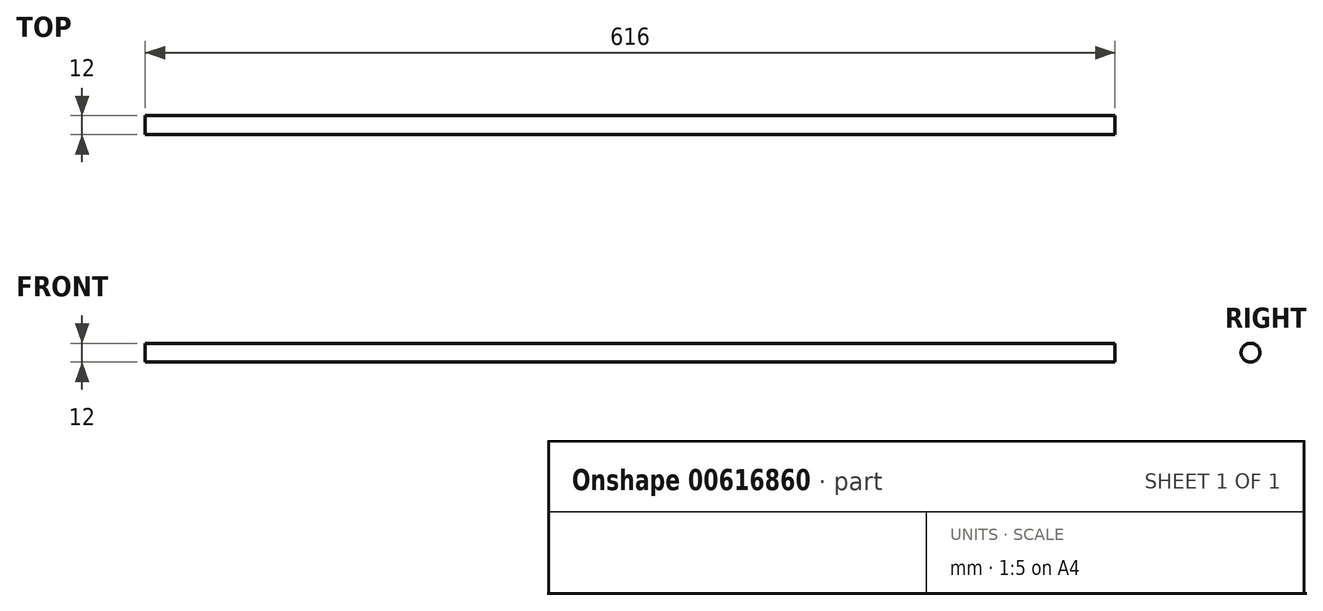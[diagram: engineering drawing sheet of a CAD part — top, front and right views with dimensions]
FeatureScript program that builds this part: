
annotation { "Feature Type Name" : "Feature", "Feature Type Description" : "" }
export const myFeature = defineFeature(function(context is Context, id is Id, definition is map)
    precondition{}
    {
        {
            var Q0;
            Q0=qCreatedBy(makeId("Right.planeOp"),FACE);
            var sketch = newSketch(context, id + "F0", { "sketchPlane" : qUnion([Q0])});
            skCircle(sketch, "E0", {"center": v(0, 0) * mm, "radius": 6 * mm});
            skSolve(sketch);
        }
        {
            var Q0;
            Q0=qSketchRegion(id+"F0",true);
            extrude(context, id + "F1", {"entities" : qUnion([Q0]), "depth" : 616 * mm, "offsetDistance" : 25 * mm, "symmetric" : true});
        }
    });
